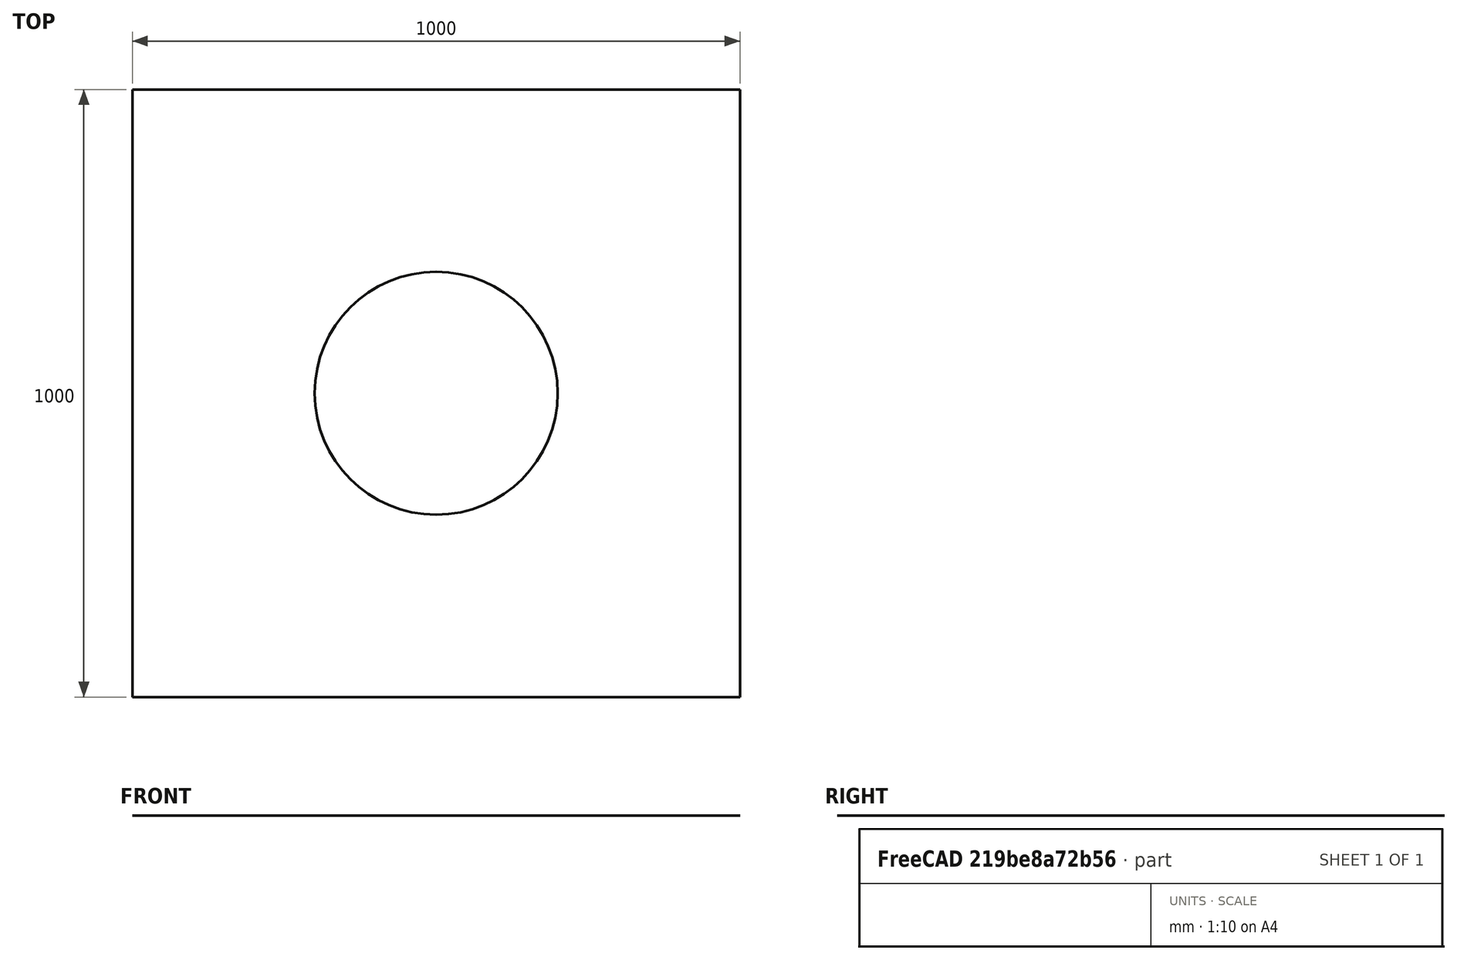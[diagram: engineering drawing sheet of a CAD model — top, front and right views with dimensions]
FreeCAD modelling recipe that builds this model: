
FCSTD DOCUMENT  (FreeCAD 0.20R29603 (Git))
Label: box_cicle_planewave
License: All rights reserved
LicenseURL: http://en.wikipedia.org/wiki/All_rights_reserved
objects: Part::Part2DObjectPython×3, App::DocumentObjectGroup×2, Part::Cut×1, Part::Feature×1, Part::FeaturePython×1
note: 6 computed .brp shape members not serialized (recipe doc carries the construction recipe); baked Part::Feature solids carry a one-line shape summary decoded from their .brp

FEATURE [Part::Part2DObjectPython] Rectangle  # Draft 2D object (typed FeaturePython)
  Area = 1e+06
  ChamferSize = 0
  Columns = 1
  FilletRadius = 0
  Height = 1000
  Length = 1000
  MakeFace = true
  Rows = 1
FEATURE [Part::Part2DObjectPython] Circle  # Draft 2D object (typed FeaturePython)
  Area = 125664
  FirstAngle = 0
  LastAngle = 0
  MakeFace = true
  Placement = pos=(500,500,0) rot=(0.862158,0.230577,0.451129;0rad)
  Radius = 200
FEATURE [Part::Cut] Cut  label="vacuum"
  Base = -> Rectangle
  Tool = -> Circle
FEATURE [Part::Feature] Part__Feature  label="inner"
  shape: bbox 400 x 400 x 2e-07 mm, 0 faces, 0 solids (baked)
FEATURE [Part::FeaturePython] Rectangle_child0  label="outer"  # WARN: FeaturePython — macro-defined, semantics opaque (R4)
  Base = -> Rectangle
  FilterType = 1
  Invert = false
  OverrideMaxVal = 0
  WindowFrom = 80
  WindowTo = 100
  items = 0
FEATURE [App::DocumentObjectGroup] Group  label="boundaries"
  Group = -> [Rectangle_child0,Part__Feature]
FEATURE [Part::Part2DObjectPython] Rectangle001  label="totalField"  # Draft 2D object (typed FeaturePython)
  Area = 640000
  ChamferSize = 0
  Columns = 1
  FilletRadius = 0
  Height = 800
  Length = 800
  MakeFace = true
  Placement = pos=(100,100,0) rot=(0,0,1;0rad)
  Rows = 1
FEATURE [App::DocumentObjectGroup] Group001  label="regions"
  Group = -> [Cut,Rectangle001]
